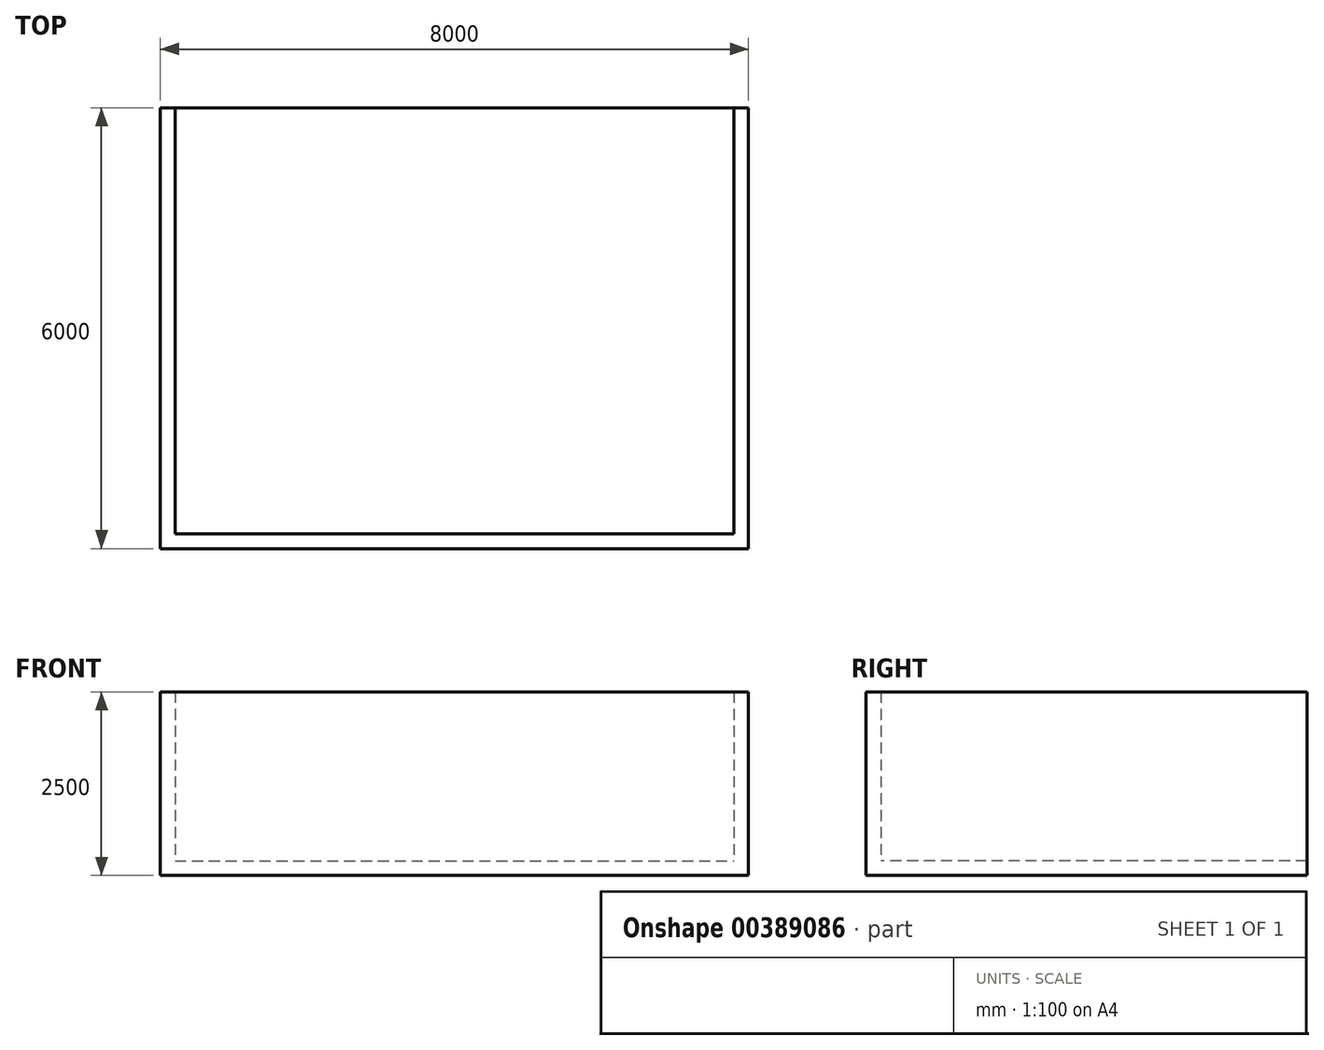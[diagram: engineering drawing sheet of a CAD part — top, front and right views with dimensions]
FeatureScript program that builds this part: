
annotation { "Feature Type Name" : "Feature", "Feature Type Description" : "" }
export const myFeature = defineFeature(function(context is Context, id is Id, definition is map)
    precondition{}
    {
        {
            var Q0;
            Q0=qCreatedBy(makeId("Top.planeOp"),FACE);
            var sketch = newSketch(context, id + "F0", { "sketchPlane" : qUnion([Q0])});
            skLineSegment(sketch, "E0.bottom", {"start": v(-95.13, 5921.08) * mm, "end": v(7904.87, 5921.08) * mm});
            skLineSegment(sketch, "E0.top", {"start": v(-95.13, -78.92) * mm, "end": v(7904.87, -78.92) * mm});
            skLineSegment(sketch, "E0.left", {"start": v(-95.13, 5921.08) * mm, "end": v(-95.13, -78.92) * mm});
            skLineSegment(sketch, "E0.right", {"start": v(7904.87, 5921.08) * mm, "end": v(7904.87, -78.92) * mm});
            skLineSegment(sketch, "E1", {"start": v(104.87, 5921.08) * mm, "end": v(104.87, -78.92) * mm});
            skLineSegment(sketch, "E2", {"start": v(7704.87, 5921.08) * mm, "end": v(7704.87, 0) * mm});
            skLineSegment(sketch, "E3", {"start": v(104.87, 121.08) * mm, "end": v(7704.87, 121.08) * mm});
            skLineSegment(sketch, "E4", {"start": v(7704.87, 0) * mm, "end": v(7704.87, -78.92) * mm});
            skLineSegment(sketch, "E5.bottom", {"start": v(3804.87, 5921.08) * mm, "end": v(4004.87, 5921.08) * mm});
            skLineSegment(sketch, "E5.top", {"start": v(3804.87, 121.08) * mm, "end": v(4004.87, 121.08) * mm});
            skLineSegment(sketch, "E5.left", {"start": v(3804.87, 5921.08) * mm, "end": v(3804.87, 121.08) * mm});
            skLineSegment(sketch, "E5.right", {"start": v(4004.87, 5921.08) * mm, "end": v(4004.87, 121.08) * mm});
            skSolve(sketch);
        }
        {
            var Q0;
            Q0=makeQuery(id+"F0.imprint","IMPRINT",FACE,{"disambiguationData":[TD([[makeQuery(id+"F0.imprint","IMPRINT",EDGE,{"derivedFrom":sQuery(id+"F0.wireOp",EDGE,"E5.bottom")}),-1.0]])]});
            var Q1;
            {var subQ4=sQuery(id+"F0.wireOp",EDGE,"E4");Q1=makeQuery(id+"F0.imprint","IMPRINT",FACE,{"disambiguationData":[TD([[makeQuery(id+"F0.imprint","IMPRINT",EDGE,{"derivedFrom":subQ4}),-1.0]])]});}
            var Q2;
            {var subQ4=sQuery(id+"F0.wireOp",EDGE,"E0.right");Q2=makeQuery(id+"F0.imprint","IMPRINT",FACE,{"disambiguationData":[TD([[makeQuery(id+"F0.imprint","IMPRINT",EDGE,{"derivedFrom":subQ4}),-1.0]])]});}
            var Q3;
            {var subQ0=sQuery(id+"F0.wireOp",EDGE,"E0.left");Q3=makeQuery(id+"F0.imprint","IMPRINT",FACE,{"disambiguationData":[TD([[makeQuery(id+"F0.imprint","IMPRINT",EDGE,{"derivedFrom":subQ0}),1.0]])]});}
            extrude(context, id + "F1", {"entities" : qUnion([Q0, Q1, Q2, Q3]), "depth" : 2500 * mm});
        }
        {
            var Q0;
            Q0 = qSketchRegion(id + "F0", true);
            extrude(context, id + "F2", {"entities" : qUnion([Q0]), "operationType" : NewBodyOperationType.ADD, "depth" : 200 * mm});
        }
    });
